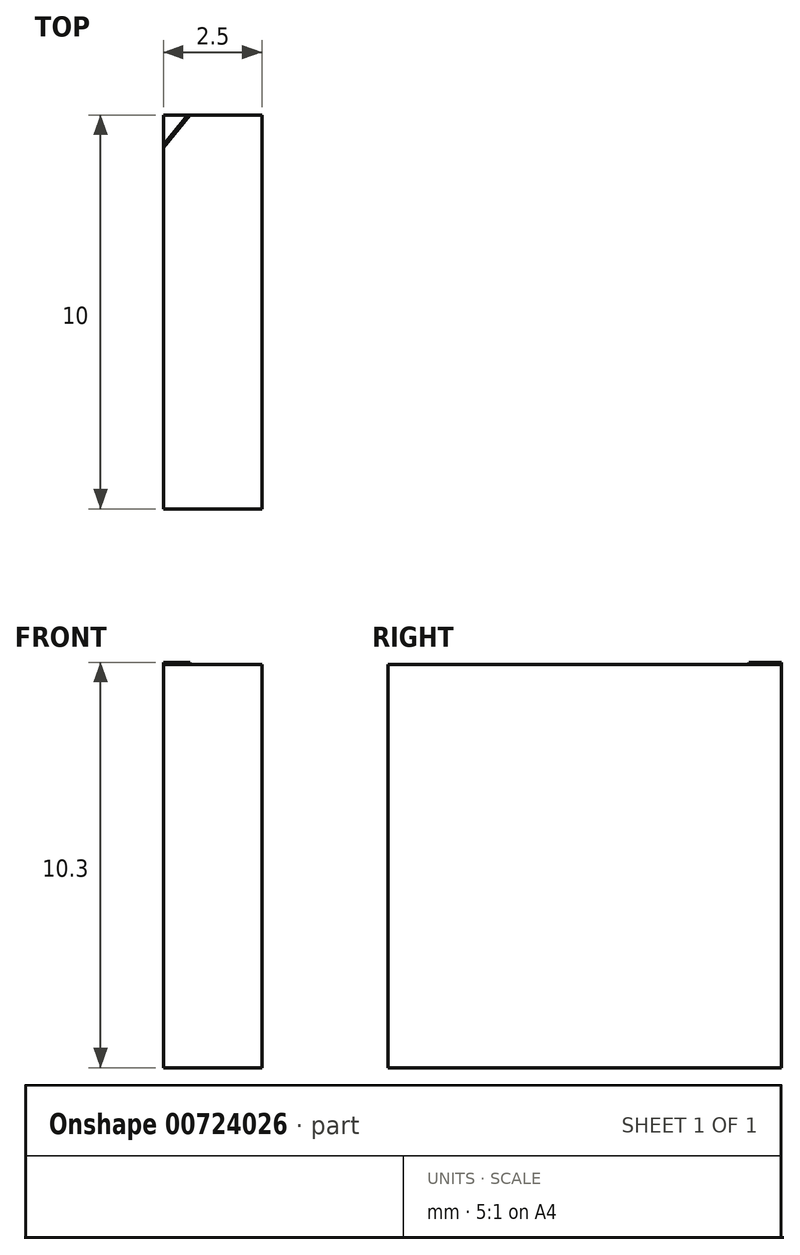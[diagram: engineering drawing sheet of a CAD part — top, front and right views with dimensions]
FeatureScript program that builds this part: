
annotation { "Feature Type Name" : "Feature", "Feature Type Description" : "" }
export const myFeature = defineFeature(function(context is Context, id is Id, definition is map)
    precondition{}
    {
        {
            var Q0;
            Q0=qCreatedBy(makeId("Right.planeOp"),FACE);
            var sketch = newSketch(context, id + "F0", { "sketchPlane" : qUnion([Q0])});
            skLineSegment(sketch, "E0.bottom", {"start": v(0, 0) * mm, "end": v(10, 0) * mm});
            skLineSegment(sketch, "E0.top", {"start": v(0, -10.25) * mm, "end": v(10, -10.25) * mm});
            skLineSegment(sketch, "E0.left", {"start": v(0, 0) * mm, "end": v(0, -10.25) * mm});
            skLineSegment(sketch, "E0.right", {"start": v(10, 0) * mm, "end": v(10, -10.25) * mm});
            skSolve(sketch);
        }
        {
            var Q0;
            Q0=makeQuery(id+"F0.imprint","IMPRINT",FACE,{"disambiguationData":[TD([[makeQuery(id+"F0.imprint","IMPRINT",EDGE,{"derivedFrom":sQuery(id+"F0.wireOp",EDGE,"E0.bottom")}),-1.0]])]});
            extrude(context, id + "F1", {"entities" : qUnion([Q0]), "depth" : 2.5 * mm, "offsetDistance" : 25 * mm});
        }
        {
            var Q0;
            Q0=qCreatedBy(makeId("Top.planeOp"),FACE);
            var sketch = newSketch(context, id + "F2", { "sketchPlane" : qUnion([Q0])});
            skLineSegment(sketch, "E1.0", {"start": v(2.5, 6.87) * mm, "end": v(0, 6.87) * mm});
            skLineSegment(sketch, "E2", {"start": v(0, 6.87) * mm, "end": v(2.47, 9.92) * mm});
            skLineSegment(sketch, "E3.0", {"start": v(1.29, 6.87) * mm, "end": v(2.5, 8.37) * mm});
            skLineSegment(sketch, "E4.0", {"start": v(0.64, 6.87) * mm, "end": v(2.5, 9.16) * mm});
            skLineSegment(sketch, "E5.0", {"start": v(1.93, 6.87) * mm, "end": v(2.5, 7.58) * mm});
            skLineSegment(sketch, "E6.0", {"start": v(0, 7.67) * mm, "end": v(1.9, 10) * mm});
            skLineSegment(sketch, "E7.0", {"start": v(0, 8.46) * mm, "end": v(1.25, 10) * mm});
            skLineSegment(sketch, "E8.0", {"start": v(0, 9.26) * mm, "end": v(0.6, 10) * mm});
            skLineSegment(sketch, "E9.0", {"start": v(2.5, 0) * mm, "end": v(2.5, 10) * mm});
            skLineSegment(sketch, "E10.0.0", {"start": v(0, 10) * mm, "end": v(0, 0) * mm});
            skLineSegment(sketch, "E10.0.1", {"start": v(0, 0) * mm, "end": v(2.5, 0) * mm});
            skLineSegment(sketch, "E10.0.3", {"start": v(2.5, 10) * mm, "end": v(0, 10) * mm});
            skLineSegment(sketch, "E11.0", {"start": v(2.5, 2.87) * mm, "end": v(0, 2.87) * mm});
            skLineSegment(sketch, "E12", {"start": v(0, 6.88) * mm, "end": v(2.5, 2.87) * mm});
            skLineSegment(sketch, "E13.0", {"start": v(0, 5.93) * mm, "end": v(1.91, 2.87) * mm});
            skLineSegment(sketch, "E14.0", {"start": v(0, 4.99) * mm, "end": v(1.32, 2.87) * mm});
            skLineSegment(sketch, "E15.0", {"start": v(0, 4.04) * mm, "end": v(0.73, 2.87) * mm});
            skLineSegment(sketch, "E16.0", {"start": v(0.59, 6.87) * mm, "end": v(2.5, 3.82) * mm});
            skLineSegment(sketch, "E17.0", {"start": v(1.27, 7.67) * mm, "end": v(1.28, 7.66) * mm});
            skLineSegment(sketch, "E18.trimOffspring", {"start": v(1.18, 6.87) * mm, "end": v(2.5, 4.76) * mm});
            skLineSegment(sketch, "E19.trimOffspring", {"start": v(1.77, 6.87) * mm, "end": v(2.5, 5.7) * mm});
            skLineSegment(sketch, "E20.0", {"start": v(0.04, 9.22) * mm, "end": v(0.64, 9.97) * mm});
            skLineSegment(sketch, "E21", {"start": v(0.64, 9.97) * mm, "end": v(0.67, 10) * mm});
            skLineSegment(sketch, "E22", {"start": v(0.04, 9.22) * mm, "end": v(0, 9.18) * mm});
            skSolve(sketch);
        }
        {
            var Q0;
            {var subQ1=sQuery(id+"F2.wireOp",EDGE,"E8.0");Q0=makeQuery(id+"F2.imprint","IMPRINT",FACE,{"disambiguationData":[TD([[makeQuery(id+"F2.imprint","IMPRINT",EDGE,{"derivedFrom":subQ1}),-1.0]])]});}
            extrude(context, id + "F3", {"entities" : qUnion([Q0]), "operationType" : NewBodyOperationType.ADD, "depth" : 0.05 * mm, "offsetDistance" : 25 * mm});
        }
    });
